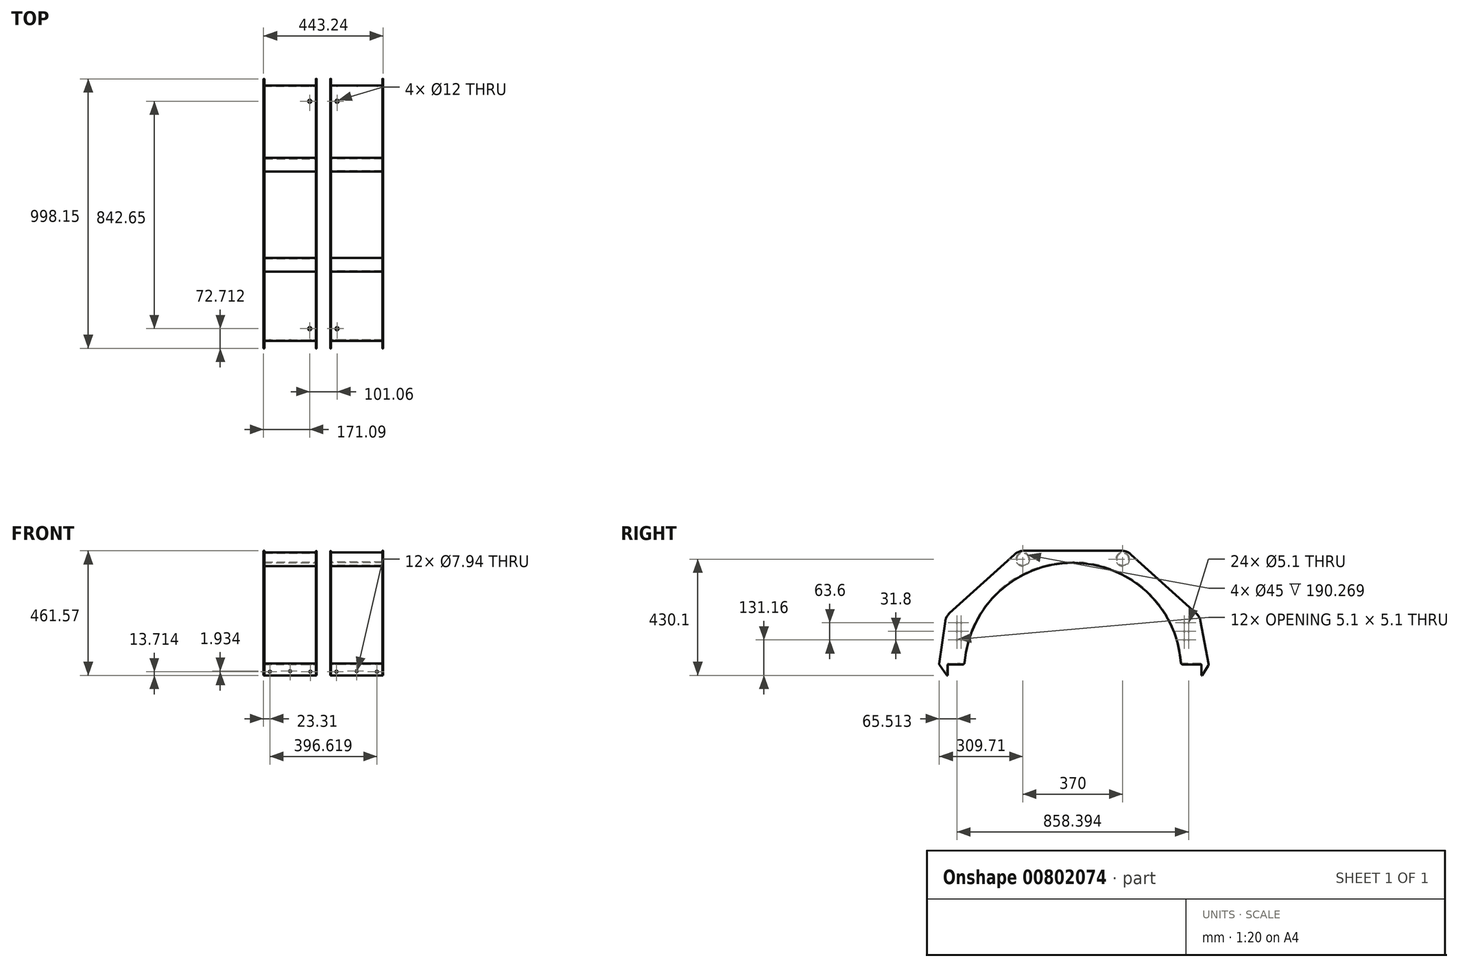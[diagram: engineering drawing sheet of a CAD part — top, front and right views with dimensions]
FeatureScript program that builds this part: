
annotation { "Feature Type Name" : "Feature", "Feature Type Description" : "" }
export const myFeature = defineFeature(function(context is Context, id is Id, definition is map)
    precondition{}
    {
        {
            var Q0;
            Q0=qCreatedBy(makeId("Right.planeOp"),FACE);
            var sketch = newSketch(context, id + "F0", { "sketchPlane" : qUnion([Q0])});
            skArc(sketch, "E0", {"start": v(-400.78, 31.26) * mm, "mid": v(0, 402) * mm, "end": v(400.78, 31.26) * mm});
            skLineSegment(sketch, "E1", {"start": v(-456.53, 215.37) * mm, "end": v(-216.59, 432.1) * mm});
            skLineSegment(sketch, "E2", {"start": v(457.5, 214.5) * mm, "end": v(216.59, 432.1) * mm});
            skLineSegment(sketch, "E3", {"start": v(183.07, 445) * mm, "end": v(-183.07, 445) * mm});
            skLineSegment(sketch, "E4", {"start": v(407.11, 25.4) * mm, "end": v(473.02, 25.4) * mm});
            skLineSegment(sketch, "E5", {"start": v(-460.32, 25.4) * mm, "end": v(-407.11, 25.4) * mm});
            skPoint(sketch, "E6.visualSharp", {"position": v(202.3, 445) * mm});
            skPoint(sketch, "E7.visualSharp", {"position": v(-401.2, 25.4) * mm});
            skArc(sketch, "E7.filletArc", {"start": v(-407.11, 25.4) * mm, "mid": v(-402.8, 27.09) * mm, "end": v(-400.78, 31.26) * mm});
            skPoint(sketch, "E8.visualSharp", {"position": v(401.2, 25.4) * mm});
            skArc(sketch, "E8.filletArc", {"start": v(400.78, 31.26) * mm, "mid": v(402.8, 27.09) * mm, "end": v(407.11, 25.4) * mm});
            skPoint(sketch, "E9.endSnap0", {"position": v(0, 402) * mm});
            skPoint(sketch, "E10", {"position": v(0, 445) * mm});
            skLineSegment(sketch, "E11", {"start": v(-472.53, 185.23) * mm, "end": v(-494.65, 27.9) * mm});
            skLineSegment(sketch, "E12", {"start": v(-493.54, 23.34) * mm, "end": v(-466.3, -15.1) * mm});
            skLineSegment(sketch, "E13", {"start": v(-463.5, -15.1) * mm, "end": v(-463.5, 22.22) * mm});
            skPoint(sketch, "E14.visualSharp", {"position": v(-470, 203.2) * mm});
            skArc(sketch, "E14.filletArc", {"start": v(-456.53, 215.37) * mm, "mid": v(-467.18, 201.7) * mm, "end": v(-472.53, 185.23) * mm});
            skPoint(sketch, "E15.visualSharp", {"position": v(-495, 25.4) * mm});
            skArc(sketch, "E15.filletArc", {"start": v(-494.65, 27.9) * mm, "mid": v(-494.53, 25.51) * mm, "end": v(-493.54, 23.34) * mm});
            skPoint(sketch, "E16.visualSharp", {"position": v(-463.5, 25.4) * mm});
            skArc(sketch, "E16.filletArc", {"start": v(-460.32, 25.4) * mm, "mid": v(-462.57, 24.47) * mm, "end": v(-463.5, 22.22) * mm});
            skLineSegment(sketch, "E17", {"start": v(476.2, 22.22) * mm, "end": v(476.2, -15.1) * mm});
            skPoint(sketch, "E18", {"position": v(505, 25.4) * mm});
            skLineSegment(sketch, "E19", {"start": v(479.37, -15.1) * mm, "end": v(502.46, 21.38) * mm});
            skLineSegment(sketch, "E20", {"start": v(503.33, 25.95) * mm, "end": v(473.12, 186.63) * mm});
            skPoint(sketch, "E21.visualSharp", {"position": v(470, 203.2) * mm});
            skArc(sketch, "E21.filletArc", {"start": v(473.12, 186.63) * mm, "mid": v(467.59, 201.85) * mm, "end": v(457.5, 214.5) * mm});
            skArc(sketch, "E22.filletArc", {"start": v(502.46, 21.38) * mm, "mid": v(503.33, 23.59) * mm, "end": v(503.33, 25.95) * mm});
            skLineSegment(sketch, "E23", {"start": v(476.2, -15.1) * mm, "end": v(479.37, -15.1) * mm});
            skLineSegment(sketch, "E24", {"start": v(-466.3, -15.1) * mm, "end": v(-463.5, -15.1) * mm});
            skPoint(sketch, "E25.visualSharp", {"position": v(476.2, 25.4) * mm});
            skArc(sketch, "E25.filletArc", {"start": v(476.2, 22.22) * mm, "mid": v(475.27, 24.47) * mm, "end": v(473.02, 25.4) * mm});
            skPoint(sketch, "E26", {"position": v(-429.2, 116.06) * mm});
            skPoint(sketch, "E27", {"position": v(-413.2, 116.06) * mm});
            skPoint(sketch, "E28", {"position": v(-413.2, 147.86) * mm});
            skPoint(sketch, "E29", {"position": v(-429.2, 147.86) * mm});
            skPoint(sketch, "E30", {"position": v(-429.2, 179.66) * mm});
            skPoint(sketch, "E31", {"position": v(-413.2, 179.66) * mm});
            skPoint(sketch, "E32", {"position": v(413.2, 179.66) * mm});
            skPoint(sketch, "E33", {"position": v(429.2, 179.66) * mm});
            skPoint(sketch, "E34", {"position": v(429.2, 147.86) * mm});
            skPoint(sketch, "E35", {"position": v(413.2, 147.86) * mm});
            skPoint(sketch, "E36", {"position": v(413.2, 116.06) * mm});
            skPoint(sketch, "E37", {"position": v(429.2, 116.06) * mm});
            skLineSegment(sketch, "E38.bottom", {"start": v(413.2, 179.66) * mm, "end": v(429.2, 179.66) * mm, "construction": true});
            skLineSegment(sketch, "E38.top", {"start": v(413.2, 116.06) * mm, "end": v(429.2, 116.06) * mm, "construction": true});
            skLineSegment(sketch, "E38.left", {"start": v(413.2, 179.66) * mm, "end": v(413.2, 116.06) * mm, "construction": true});
            skLineSegment(sketch, "E38.right", {"start": v(429.2, 179.66) * mm, "end": v(429.2, 116.06) * mm, "construction": true});
            skLineSegment(sketch, "E39", {"start": v(0, 0) * mm, "end": v(0, 524.96) * mm, "construction": true});
            skPoint(sketch, "E40.visualSharp", {"position": v(-202.31, 445) * mm});
            skArc(sketch, "E40.filletArc", {"start": v(-183.07, 445) * mm, "mid": v(-201.03, 441.66) * mm, "end": v(-216.59, 432.1) * mm});
            skPoint(sketch, "E41.newPointB", {"position": v(202.31, 445) * mm});
            skArc(sketch, "E41.filletArc", {"start": v(216.59, 432.1) * mm, "mid": v(201.03, 441.66) * mm, "end": v(183.07, 445) * mm});
            skSolve(sketch);
        }
        {
            var Q0;
            Q0 = qSketchRegion(id + "F0", true);
            extrude(context, id + "F1", {"entities" : qUnion([Q0]), "depth" : 3.17 * mm});
        }
        {
            var Q0;
            Q0=makeQuery(id+"F1.opExtrude","CAP_FACE",FACE,{"disambiguationData":[OSD([sQuery(id+"F0.wireOp",EDGE,"E0"),sQuery(id+"F0.wireOp",EDGE,"E9loCTzL-wOmK-y6Et-Pe2N-kgU0UY5jq1ZF"),sQuery(id+"F0.wireOp",EDGE,"E1"),sQuery(id+"F0.wireOp",EDGE,"s9JNnq10-T5jz-dtBx-Jel8-L66kQnyxZmdq"),sQuery(id+"F0.wireOp",EDGE,"E2"),sQuery(id+"F0.wireOp",EDGE,"E3"),sQuery(id+"F0.wireOp",EDGE,"E4"),sQuery(id+"F0.wireOp",EDGE,"E5"),sQuery(id+"F0.wireOp",EDGE,"86fa77fb-b35d-4607-8103-cc9440c46565.filletArc"),sQuery(id+"F0.wireOp",EDGE,"56854ff8-0e41-4e1b-8477-ec3efaea42f3.filletArc"),sQuery(id+"F0.wireOp",EDGE,"E6.filletArc"),sQuery(id+"F0.wireOp",EDGE,"a73865e9-f12d-4e8d-86f3-43cc75951e77.filletArc")])],"isStart":false});
            var sketch = newSketch(context, id + "F2", { "sketchPlane" : qUnion([Q0])});
            skArc(sketch, "E42", {"start": v(-400.78, 31.26) * mm, "mid": v(0, 402) * mm, "end": v(400.78, 31.26) * mm});
            skArc(sketch, "E43", {"start": v(-403.95, 31.5) * mm, "mid": v(0, 405.18) * mm, "end": v(403.95, 31.5) * mm});
            skLineSegment(sketch, "E44", {"start": v(-460.32, 28.57) * mm, "end": v(-407.11, 28.57) * mm});
            skLineSegment(sketch, "E45", {"start": v(-460.32, 25.4) * mm, "end": v(-407.11, 25.4) * mm});
            skArc(sketch, "E46.filletArc", {"start": v(-407.11, 25.4) * mm, "mid": v(-402.8, 27.09) * mm, "end": v(-400.78, 31.26) * mm});
            skArc(sketch, "E47.filletArc", {"start": v(-407.11, 28.57) * mm, "mid": v(-404.96, 29.42) * mm, "end": v(-403.95, 31.5) * mm});
            skLineSegment(sketch, "E48", {"start": v(473.02, 28.58) * mm, "end": v(407.11, 28.57) * mm});
            skLineSegment(sketch, "E49", {"start": v(473.02, 25.4) * mm, "end": v(407.11, 25.4) * mm});
            skArc(sketch, "E50.filletArc", {"start": v(400.78, 31.26) * mm, "mid": v(402.8, 27.09) * mm, "end": v(407.11, 25.4) * mm});
            skArc(sketch, "E51.filletArc", {"start": v(403.95, 31.5) * mm, "mid": v(404.96, 29.42) * mm, "end": v(407.11, 28.57) * mm});
            skLineSegment(sketch, "E52", {"start": v(-466.67, 22.22) * mm, "end": v(-466.67, -15.1) * mm});
            skLineSegment(sketch, "E53", {"start": v(-463.5, 22.22) * mm, "end": v(-463.5, -15.1) * mm});
            skLineSegment(sketch, "E54", {"start": v(-463.5, -15.1) * mm, "end": v(-466.67, -15.1) * mm});
            skPoint(sketch, "E55.visualSharp", {"position": v(-463.5, 25.4) * mm});
            skArc(sketch, "E55.filletArc", {"start": v(-460.32, 25.4) * mm, "mid": v(-462.57, 24.47) * mm, "end": v(-463.5, 22.22) * mm});
            skPoint(sketch, "E56.visualSharp", {"position": v(-466.67, 28.57) * mm});
            skArc(sketch, "E56.filletArc", {"start": v(-460.32, 28.57) * mm, "mid": v(-464.81, 26.72) * mm, "end": v(-466.67, 22.22) * mm});
            skLineSegment(sketch, "E57", {"start": v(476.2, 22.23) * mm, "end": v(476.2, -15.1) * mm});
            skLineSegment(sketch, "E58", {"start": v(476.2, -15.1) * mm, "end": v(479.37, -15.1) * mm});
            skLineSegment(sketch, "E59", {"start": v(479.37, -15.1) * mm, "end": v(479.37, 22.23) * mm});
            skPoint(sketch, "E60.visualSharp", {"position": v(476.2, 25.4) * mm});
            skArc(sketch, "E60.filletArc", {"start": v(476.2, 22.23) * mm, "mid": v(475.27, 24.47) * mm, "end": v(473.02, 25.4) * mm});
            skPoint(sketch, "E61.visualSharp", {"position": v(479.37, 28.58) * mm});
            skArc(sketch, "E61.filletArc", {"start": v(479.37, 22.23) * mm, "mid": v(477.51, 26.72) * mm, "end": v(473.02, 28.58) * mm});
            skSolve(sketch);
        }
        {
            var Q0;
            Q0 = qSketchRegion(id + "F2", true);
            extrude(context, id + "F3", {"entities" : qUnion([Q0]), "operationType" : NewBodyOperationType.ADD, "depth" : 190.27 * mm});
        }
        {
            var Q0;
            Q0=makeQuery(id+"F3.opExtrude","CAP_FACE",FACE,{"disambiguationData":[OSD([sQuery(id+"F2.wireOp",EDGE,"E42"),sQuery(id+"F2.wireOp",EDGE,"E43"),sQuery(id+"F2.wireOp",EDGE,"Qj5uD3Kj-Tnei-hYOQ-ZmSB-v0AgtbXvPEYO"),sQuery(id+"F2.wireOp",EDGE,"4pAmY6wd-Oeoi-wrFi-XpuQ-VInCCUa1Rv9z")])],"isStart":false});
            var sketch = newSketch(context, id + "F4", { "sketchPlane" : qUnion([Q0])});
            skArc(sketch, "E62", {"start": v(-400.78, 31.26) * mm, "mid": v(0, 402) * mm, "end": v(400.78, 31.26) * mm});
            skLineSegment(sketch, "E63", {"start": v(-456.31, 215.56) * mm, "end": v(-215.19, 433.37) * mm});
            skLineSegment(sketch, "E64", {"start": v(457.3, 214.68) * mm, "end": v(215.19, 433.37) * mm});
            skLineSegment(sketch, "E65", {"start": v(181.14, 446.47) * mm, "end": v(-181.14, 446.47) * mm});
            skPoint(sketch, "E66.visualSharp", {"position": v(-200.68, 446.47) * mm});
            skArc(sketch, "E66.filletArc", {"start": v(-181.14, 446.47) * mm, "mid": v(-199.38, 443.08) * mm, "end": v(-215.19, 433.37) * mm});
            skPoint(sketch, "E67.visualSharp", {"position": v(200.68, 446.47) * mm});
            skArc(sketch, "E67.filletArc", {"start": v(215.19, 433.37) * mm, "mid": v(199.38, 443.08) * mm, "end": v(181.14, 446.47) * mm});
            skPoint(sketch, "E68.visualSharp", {"position": v(398.78, 50.8) * mm});
            skLineSegment(sketch, "E69", {"start": v(0, 0) * mm, "end": v(0.42, 473.33) * mm, "construction": true});
            skPoint(sketch, "E69.endSnap0", {"position": v(0.42, 402) * mm});
            skLineSegment(sketch, "E70", {"start": v(-472.57, 184.94) * mm, "end": v(-494.65, 27.9) * mm});
            skArc(sketch, "E71.filletArc", {"start": v(-456.31, 215.56) * mm, "mid": v(-467.13, 201.68) * mm, "end": v(-472.57, 184.94) * mm});
            skLineSegment(sketch, "E72", {"start": v(473.17, 186.37) * mm, "end": v(503.33, 25.95) * mm});
            skArc(sketch, "E73.filletArc", {"start": v(473.17, 186.37) * mm, "mid": v(467.55, 201.83) * mm, "end": v(457.3, 214.68) * mm});
            skLineSegment(sketch, "E74", {"start": v(407.11, 25.4) * mm, "end": v(473.02, 25.4) * mm});
            skPoint(sketch, "E74.endSnap0", {"position": v(440.07, 25.4) * mm});
            skLineSegment(sketch, "E75", {"start": v(476.2, 22.22) * mm, "end": v(476.2, -15.1) * mm});
            skPoint(sketch, "E76.newPointA", {"position": v(481.52, 25.4) * mm});
            skArc(sketch, "E76.filletArc", {"start": v(476.2, 22.22) * mm, "mid": v(475.27, 24.47) * mm, "end": v(473.02, 25.4) * mm});
            skLineSegment(sketch, "E77", {"start": v(-407.11, 25.4) * mm, "end": v(-460.32, 25.4) * mm});
            skArc(sketch, "E78.filletArc", {"start": v(502.46, 21.38) * mm, "mid": v(503.33, 23.59) * mm, "end": v(503.33, 25.95) * mm});
            skLineSegment(sketch, "E79", {"start": v(-463.5, 22.22) * mm, "end": v(-463.5, -14.56) * mm});
            skLineSegment(sketch, "E80", {"start": v(-493.54, 23.34) * mm, "end": v(-466.67, -14.56) * mm});
            skPoint(sketch, "E81.newPointA", {"position": v(-497.1, 28.36) * mm});
            skPoint(sketch, "E81.newPointB", {"position": v(-494.58, 28.36) * mm});
            skArc(sketch, "E81.filletArc", {"start": v(-494.65, 27.9) * mm, "mid": v(-494.53, 25.51) * mm, "end": v(-493.54, 23.34) * mm});
            skArc(sketch, "E82.filletArc", {"start": v(-407.11, 25.4) * mm, "mid": v(-402.8, 27.09) * mm, "end": v(-400.78, 31.26) * mm});
            skArc(sketch, "E83.filletArc", {"start": v(400.78, 31.26) * mm, "mid": v(402.8, 27.09) * mm, "end": v(407.11, 25.4) * mm});
            skArc(sketch, "E84.filletArc", {"start": v(-460.32, 25.4) * mm, "mid": v(-462.57, 24.47) * mm, "end": v(-463.5, 22.22) * mm});
            skLineSegment(sketch, "E85", {"start": v(479.37, -15.1) * mm, "end": v(476.2, -15.1) * mm});
            skLineSegment(sketch, "E86.trimOffspring", {"start": v(479.37, -15.1) * mm, "end": v(502.46, 21.38) * mm});
            skLineSegment(sketch, "E87", {"start": v(-466.67, -14.56) * mm, "end": v(-463.5, -14.56) * mm});
            skSolve(sketch);
        }
        {
            var Q0;
            Q0 = qSketchRegion(id + "F4", true);
            extrude(context, id + "F5", {"entities" : qUnion([Q0]), "operationType" : NewBodyOperationType.ADD, "depth" : 3.17 * mm});
        }
        {
            var Q0;
            Q0=makeQuery(id+"F1.opExtrude","CAP_FACE",FACE,{"disambiguationData":[OSD([sQuery(id+"F0.wireOp",EDGE,"E0"),sQuery(id+"F0.wireOp",EDGE,"E9loCTzL-wOmK-y6Et-Pe2N-kgU0UY5jq1ZF"),sQuery(id+"F0.wireOp",EDGE,"E1"),sQuery(id+"F0.wireOp",EDGE,"s9JNnq10-T5jz-dtBx-Jel8-L66kQnyxZmdq"),sQuery(id+"F0.wireOp",EDGE,"E2"),sQuery(id+"F0.wireOp",EDGE,"E3"),sQuery(id+"F0.wireOp",EDGE,"E4"),sQuery(id+"F0.wireOp",EDGE,"E5"),sQuery(id+"F0.wireOp",EDGE,"86fa77fb-b35d-4607-8103-cc9440c46565.filletArc"),sQuery(id+"F0.wireOp",EDGE,"56854ff8-0e41-4e1b-8477-ec3efaea42f3.filletArc"),sQuery(id+"F0.wireOp",EDGE,"E6.filletArc"),sQuery(id+"F0.wireOp",EDGE,"a73865e9-f12d-4e8d-86f3-43cc75951e77.filletArc")])],"isStart":false});
            var sketch = newSketch(context, id + "F6", { "sketchPlane" : qUnion([Q0])});
            skCircle(sketch, "E88", {"center": v(185, 415) * mm, "radius": 25.4 * mm});
            skCircle(sketch, "E89", {"center": v(185, 415) * mm, "radius": 22.5 * mm});
            skCircle(sketch, "E90", {"center": v(-185, 415) * mm, "radius": 25.4 * mm});
            skCircle(sketch, "E91", {"center": v(-185, 415) * mm, "radius": 22.5 * mm});
            skSolve(sketch);
        }
        {
            var Q0;
            Q0 = qSketchRegion(id + "F6", true);
            extrude(context, id + "F7", {"entities" : qUnion([Q0]), "operationType" : NewBodyOperationType.ADD, "depth" : 190.27 * mm});
        }
        {
            var Q0;
            Q0=sQuery(id+"F0.wireOp",VERTEX,"E33");
            var Q1;
            Q1=sQuery(id+"F0.wireOp",VERTEX,"E32");
            var Q2;
            Q2=sQuery(id+"F0.wireOp",VERTEX,"E35");
            var Q3;
            Q3=sQuery(id+"F0.wireOp",VERTEX,"E34");
            var Q4;
            Q4=sQuery(id+"F0.wireOp",VERTEX,"E37");
            var Q5;
            Q5=sQuery(id+"F0.wireOp",VERTEX,"E36");
            var Q6;
            Q6=sQuery(id+"F0.wireOp",VERTEX,"E31");
            var Q7;
            Q7=sQuery(id+"F0.wireOp",VERTEX,"E30");
            var Q8;
            Q8=sQuery(id+"F0.wireOp",VERTEX,"E29");
            var Q9;
            Q9=sQuery(id+"F0.wireOp",VERTEX,"E28");
            var Q10;
            Q10=sQuery(id+"F0.wireOp",VERTEX,"E27");
            var Q11;
            Q11=sQuery(id+"F0.wireOp",VERTEX,"E26");
            var Q12;
            Q12=makeQuery(id+"F1.opExtrude","SWEPT_BODY",BODY,{"disambiguationData":[OSD([sQuery(id+"F0.wireOp",EDGE,"E0"),sQuery(id+"F0.wireOp",EDGE,"E1"),sQuery(id+"F0.wireOp",EDGE,"E2"),sQuery(id+"F0.wireOp",EDGE,"E3"),sQuery(id+"F0.wireOp",EDGE,"E4"),sQuery(id+"F0.wireOp",EDGE,"E5"),sQuery(id+"F0.wireOp",EDGE,"56854ff8-0e41-4e1b-8477-ec3efaea42f3.filletArc"),sQuery(id+"F0.wireOp",EDGE,"E6.filletArc"),sQuery(id+"F0.wireOp",EDGE,"E7.filletArc"),sQuery(id+"F0.wireOp",EDGE,"E8.filletArc"),sQuery(id+"F0.wireOp",EDGE,"E11"),sQuery(id+"F0.wireOp",EDGE,"E12"),sQuery(id+"F0.wireOp",EDGE,"E13"),sQuery(id+"F0.wireOp",EDGE,"E14.filletArc"),sQuery(id+"F0.wireOp",EDGE,"E15.filletArc"),sQuery(id+"F0.wireOp",EDGE,"E16.filletArc"),sQuery(id+"F0.wireOp",EDGE,"E17"),sQuery(id+"F0.wireOp",EDGE,"E19"),sQuery(id+"F0.wireOp",EDGE,"E20"),sQuery(id+"F0.wireOp",EDGE,"E21.filletArc"),sQuery(id+"F0.wireOp",EDGE,"E22.filletArc"),sQuery(id+"F0.wireOp",EDGE,"E23"),sQuery(id+"F0.wireOp",EDGE,"E24"),sQuery(id+"F0.wireOp",EDGE,"E25.filletArc")])]});
            hole(context, id + "F8", {"style" : HoleStyle.SIMPLE, "endStyle" : HoleEndStyle.BLIND, "oppositeDirection" : true, "holeDiameter" : 5.1 * mm, "holeDepth" : 17.75 * mm, "isTappedThrough" : true, "tappedDepth" : 10.25 * mm, "tapClearance" : 3, "startFromSketch" : true, "locations" : qUnion([Q0, Q1, Q2, Q3, Q4, Q5, Q6, Q7, Q8, Q9, Q10, Q11]), "scope" : qUnion([Q12])});
        }
        {
            var Q0;
            Q0=qCreatedBy(makeId("Right.planeOp"),FACE);
            cPlane(context, id + "F9", {"entities" : qUnion([Q0]), "cplaneType" : CPlaneType.OFFSET, "offset" : 25 * mm, "oppositeDirection" : true, "width" : 150 * mm, "height" : 150 * mm});
        }
        {
            var Q0;
            Q0=makeQuery(id+"F1.opExtrude","SWEPT_BODY",BODY,{"disambiguationData":[OSD([sQuery(id+"F0.wireOp",EDGE,"E0"),sQuery(id+"F0.wireOp",EDGE,"E1"),sQuery(id+"F0.wireOp",EDGE,"E2"),sQuery(id+"F0.wireOp",EDGE,"E3"),sQuery(id+"F0.wireOp",EDGE,"E4"),sQuery(id+"F0.wireOp",EDGE,"E5"),sQuery(id+"F0.wireOp",EDGE,"56854ff8-0e41-4e1b-8477-ec3efaea42f3.filletArc"),sQuery(id+"F0.wireOp",EDGE,"E6.filletArc"),sQuery(id+"F0.wireOp",EDGE,"E7.filletArc"),sQuery(id+"F0.wireOp",EDGE,"E8.filletArc"),sQuery(id+"F0.wireOp",EDGE,"E11"),sQuery(id+"F0.wireOp",EDGE,"E12"),sQuery(id+"F0.wireOp",EDGE,"E13"),sQuery(id+"F0.wireOp",EDGE,"E14.filletArc"),sQuery(id+"F0.wireOp",EDGE,"E15.filletArc"),sQuery(id+"F0.wireOp",EDGE,"E16.filletArc"),sQuery(id+"F0.wireOp",EDGE,"E17"),sQuery(id+"F0.wireOp",EDGE,"E19"),sQuery(id+"F0.wireOp",EDGE,"E20"),sQuery(id+"F0.wireOp",EDGE,"E21.filletArc"),sQuery(id+"F0.wireOp",EDGE,"E22.filletArc"),sQuery(id+"F0.wireOp",EDGE,"E23"),sQuery(id+"F0.wireOp",EDGE,"E24"),sQuery(id+"F0.wireOp",EDGE,"E25.filletArc")])]});
            var Q1;
            Q1=qCreatedBy(id+"F9.planeOp",FACE);
            mirror(context, id + "F10", {"entities" : qUnion([Q0]), "mirrorPlane" : qUnion([Q1])});
        }
        {
            var Q0;
            Q0=makeQuery(id+"F10.opPattern","COPY",BODY,{"derivedFrom":makeQuery(id+"F1.opExtrude","SWEPT_BODY",BODY,{"disambiguationData":[OSD([sQuery(id+"F0.wireOp",EDGE,"E0"),sQuery(id+"F0.wireOp",EDGE,"E1"),sQuery(id+"F0.wireOp",EDGE,"E2"),sQuery(id+"F0.wireOp",EDGE,"E3"),sQuery(id+"F0.wireOp",EDGE,"E4"),sQuery(id+"F0.wireOp",EDGE,"E5"),sQuery(id+"F0.wireOp",EDGE,"56854ff8-0e41-4e1b-8477-ec3efaea42f3.filletArc"),sQuery(id+"F0.wireOp",EDGE,"E6.filletArc"),sQuery(id+"F0.wireOp",EDGE,"E7.filletArc"),sQuery(id+"F0.wireOp",EDGE,"E8.filletArc"),sQuery(id+"F0.wireOp",EDGE,"E11"),sQuery(id+"F0.wireOp",EDGE,"E12"),sQuery(id+"F0.wireOp",EDGE,"E13"),sQuery(id+"F0.wireOp",EDGE,"E14.filletArc"),sQuery(id+"F0.wireOp",EDGE,"E15.filletArc"),sQuery(id+"F0.wireOp",EDGE,"E16.filletArc"),sQuery(id+"F0.wireOp",EDGE,"E17"),sQuery(id+"F0.wireOp",EDGE,"E19"),sQuery(id+"F0.wireOp",EDGE,"E20"),sQuery(id+"F0.wireOp",EDGE,"E21.filletArc"),sQuery(id+"F0.wireOp",EDGE,"E22.filletArc"),sQuery(id+"F0.wireOp",EDGE,"E23"),sQuery(id+"F0.wireOp",EDGE,"E24"),sQuery(id+"F0.wireOp",EDGE,"E25.filletArc")])]}),"instanceName":"1"});
            deleteBodies(context, id + "F11", {"entities" : qUnion([Q0])});
        }
        {
            var Q0;
            Q0=makeQuery(id+"F3.opExtrude","SWEPT_FACE",FACE,{"disambiguationData":[OSD([sQuery(id+"F2.wireOp",EDGE,"E52")])]});
            var sketch = newSketch(context, id + "F12", { "sketchPlane" : qUnion([Q0])});
            skLineSegment(sketch, "E92", {"start": v(-18.58, -1.39) * mm, "end": v(188.45, -1.39) * mm, "construction": true});
            skLineSegment(sketch, "E93", {"start": v(23.3, -19.94) * mm, "end": v(23.3, 12.68) * mm, "construction": true});
            skLineSegment(sketch, "E94", {"start": v(173.3, -20.85) * mm, "end": v(173.3, 12.98) * mm, "construction": true});
            skPoint(sketch, "E95", {"position": v(23.3, -1.39) * mm});
            skPoint(sketch, "E96", {"position": v(98.3, -1.39) * mm});
            skPoint(sketch, "E97", {"position": v(173.3, -1.39) * mm});
            skPoint(sketch, "E98", {"position": v(98.3, 0.55) * mm});
            skSolve(sketch);
        }
        {
            var Q0;
            Q0=sQuery(id+"F12.wireOp",VERTEX,"E95");
            var Q1;
            Q1=sQuery(id+"F12.wireOp",VERTEX,"E97");
            var Q2;
            Q2=sQuery(id+"F12.wireOp",VERTEX,"E98");
            var Q3;
            Q3=makeQuery(id+"F1.opExtrude","SWEPT_BODY",BODY,{"disambiguationData":[OSD([sQuery(id+"F0.wireOp",EDGE,"E0"),sQuery(id+"F0.wireOp",EDGE,"E1"),sQuery(id+"F0.wireOp",EDGE,"E2"),sQuery(id+"F0.wireOp",EDGE,"E3"),sQuery(id+"F0.wireOp",EDGE,"E4"),sQuery(id+"F0.wireOp",EDGE,"E5"),sQuery(id+"F0.wireOp",EDGE,"56854ff8-0e41-4e1b-8477-ec3efaea42f3.filletArc"),sQuery(id+"F0.wireOp",EDGE,"E6.filletArc"),sQuery(id+"F0.wireOp",EDGE,"E7.filletArc"),sQuery(id+"F0.wireOp",EDGE,"E8.filletArc"),sQuery(id+"F0.wireOp",EDGE,"E11"),sQuery(id+"F0.wireOp",EDGE,"E12"),sQuery(id+"F0.wireOp",EDGE,"E13"),sQuery(id+"F0.wireOp",EDGE,"E14.filletArc"),sQuery(id+"F0.wireOp",EDGE,"E15.filletArc"),sQuery(id+"F0.wireOp",EDGE,"E16.filletArc"),sQuery(id+"F0.wireOp",EDGE,"E17"),sQuery(id+"F0.wireOp",EDGE,"E19"),sQuery(id+"F0.wireOp",EDGE,"E20"),sQuery(id+"F0.wireOp",EDGE,"E21.filletArc"),sQuery(id+"F0.wireOp",EDGE,"E22.filletArc"),sQuery(id+"F0.wireOp",EDGE,"E23"),sQuery(id+"F0.wireOp",EDGE,"E24"),sQuery(id+"F0.wireOp",EDGE,"E25.filletArc")])]});
            hole(context, id + "F13", {"style" : HoleStyle.SIMPLE, "endStyle" : HoleEndStyle.THROUGH, "holeDiameter" : 7.94 * mm, "isTappedThrough" : true, "tappedDepth" : 10.25 * mm, "tapClearance" : 3, "startFromSketch" : true, "locations" : qUnion([Q0, Q1, Q2]), "scope" : qUnion([Q3]), "majorDiameter" : 5 * mm});
        }
        {
            var Q0;
            Q0=makeQuery(id+"F1.opExtrude","SWEPT_BODY",BODY,{"disambiguationData":[OSD([sQuery(id+"F0.wireOp",EDGE,"E0"),sQuery(id+"F0.wireOp",EDGE,"E1"),sQuery(id+"F0.wireOp",EDGE,"E2"),sQuery(id+"F0.wireOp",EDGE,"E3"),sQuery(id+"F0.wireOp",EDGE,"E4"),sQuery(id+"F0.wireOp",EDGE,"E5"),sQuery(id+"F0.wireOp",EDGE,"56854ff8-0e41-4e1b-8477-ec3efaea42f3.filletArc"),sQuery(id+"F0.wireOp",EDGE,"E6.filletArc"),sQuery(id+"F0.wireOp",EDGE,"E7.filletArc"),sQuery(id+"F0.wireOp",EDGE,"E8.filletArc"),sQuery(id+"F0.wireOp",EDGE,"E11"),sQuery(id+"F0.wireOp",EDGE,"E12"),sQuery(id+"F0.wireOp",EDGE,"E13"),sQuery(id+"F0.wireOp",EDGE,"E14.filletArc"),sQuery(id+"F0.wireOp",EDGE,"E15.filletArc"),sQuery(id+"F0.wireOp",EDGE,"E16.filletArc"),sQuery(id+"F0.wireOp",EDGE,"E17"),sQuery(id+"F0.wireOp",EDGE,"E19"),sQuery(id+"F0.wireOp",EDGE,"E20"),sQuery(id+"F0.wireOp",EDGE,"E21.filletArc"),sQuery(id+"F0.wireOp",EDGE,"E22.filletArc"),sQuery(id+"F0.wireOp",EDGE,"E23"),sQuery(id+"F0.wireOp",EDGE,"E24"),sQuery(id+"F0.wireOp",EDGE,"E25.filletArc")])]});
            var Q1;
            Q1=qCreatedBy(id+"F9.planeOp",FACE);
            mirror(context, id + "F14", {"entities" : qUnion([Q0]), "mirrorPlane" : qUnion([Q1])});
        }
        {
            var Q0;
            Q0=makeQuery(id+"F3.opExtrude","SWEPT_FACE",FACE,{"disambiguationData":[OSD([sQuery(id+"F2.wireOp",EDGE,"E44")])]});
            var sketch = newSketch(context, id + "F15", { "sketchPlane" : qUnion([Q0])});
            skCircle(sketch, "E99", {"center": v(25.53, -422) * mm, "radius": 6 * mm});
            skSolve(sketch);
        }
        {
            var Q0;
            Q0 = qSketchRegion(id + "F15", true);
            extrude(context, id + "F16", {"entities" : qUnion([Q0]), "operationType" : NewBodyOperationType.REMOVE, "oppositeDirection" : true, "depth" : 25 * mm});
        }
        {
            var Q0;
            Q0=makeQuery(id+"F3.opExtrude","SWEPT_FACE",FACE,{"disambiguationData":[OSD([sQuery(id+"F2.wireOp",EDGE,"E48")])]});
            var sketch = newSketch(context, id + "F17", { "sketchPlane" : qUnion([Q0])});
            skCircle(sketch, "E100", {"center": v(25.53, 420.65) * mm, "radius": 6 * mm});
            skSolve(sketch);
        }
        {
            var Q0;
            Q0 = qSketchRegion(id + "F17", true);
            extrude(context, id + "F18", {"entities" : qUnion([Q0]), "operationType" : NewBodyOperationType.REMOVE, "oppositeDirection" : true, "depth" : 25 * mm});
        }
        {
            var Q0;
            Q0=makeQuery(id+"F14.opPattern","COPY",BODY,{"derivedFrom":makeQuery(id+"F1.opExtrude","SWEPT_BODY",BODY,{"disambiguationData":[OSD([sQuery(id+"F0.wireOp",EDGE,"E0"),sQuery(id+"F0.wireOp",EDGE,"E1"),sQuery(id+"F0.wireOp",EDGE,"E2"),sQuery(id+"F0.wireOp",EDGE,"E3"),sQuery(id+"F0.wireOp",EDGE,"E4"),sQuery(id+"F0.wireOp",EDGE,"E5"),sQuery(id+"F0.wireOp",EDGE,"56854ff8-0e41-4e1b-8477-ec3efaea42f3.filletArc"),sQuery(id+"F0.wireOp",EDGE,"E6.filletArc"),sQuery(id+"F0.wireOp",EDGE,"E7.filletArc"),sQuery(id+"F0.wireOp",EDGE,"E8.filletArc"),sQuery(id+"F0.wireOp",EDGE,"E11"),sQuery(id+"F0.wireOp",EDGE,"E12"),sQuery(id+"F0.wireOp",EDGE,"E13"),sQuery(id+"F0.wireOp",EDGE,"E14.filletArc"),sQuery(id+"F0.wireOp",EDGE,"E15.filletArc"),sQuery(id+"F0.wireOp",EDGE,"E16.filletArc"),sQuery(id+"F0.wireOp",EDGE,"E17"),sQuery(id+"F0.wireOp",EDGE,"E19"),sQuery(id+"F0.wireOp",EDGE,"E20"),sQuery(id+"F0.wireOp",EDGE,"E21.filletArc"),sQuery(id+"F0.wireOp",EDGE,"E22.filletArc"),sQuery(id+"F0.wireOp",EDGE,"E23"),sQuery(id+"F0.wireOp",EDGE,"E24"),sQuery(id+"F0.wireOp",EDGE,"E25.filletArc")])]}),"instanceName":"1"});
            deleteBodies(context, id + "F19", {"entities" : qUnion([Q0])});
        }
        {
            var Q0;
            Q0=makeQuery(id+"F1.opExtrude","SWEPT_BODY",BODY,{"disambiguationData":[OSD([sQuery(id+"F0.wireOp",EDGE,"E0"),sQuery(id+"F0.wireOp",EDGE,"E1"),sQuery(id+"F0.wireOp",EDGE,"E2"),sQuery(id+"F0.wireOp",EDGE,"E3"),sQuery(id+"F0.wireOp",EDGE,"E4"),sQuery(id+"F0.wireOp",EDGE,"E5"),sQuery(id+"F0.wireOp",EDGE,"56854ff8-0e41-4e1b-8477-ec3efaea42f3.filletArc"),sQuery(id+"F0.wireOp",EDGE,"E6.filletArc"),sQuery(id+"F0.wireOp",EDGE,"E7.filletArc"),sQuery(id+"F0.wireOp",EDGE,"E8.filletArc"),sQuery(id+"F0.wireOp",EDGE,"E11"),sQuery(id+"F0.wireOp",EDGE,"E12"),sQuery(id+"F0.wireOp",EDGE,"E13"),sQuery(id+"F0.wireOp",EDGE,"E14.filletArc"),sQuery(id+"F0.wireOp",EDGE,"E15.filletArc"),sQuery(id+"F0.wireOp",EDGE,"E16.filletArc"),sQuery(id+"F0.wireOp",EDGE,"E17"),sQuery(id+"F0.wireOp",EDGE,"E19"),sQuery(id+"F0.wireOp",EDGE,"E20"),sQuery(id+"F0.wireOp",EDGE,"E21.filletArc"),sQuery(id+"F0.wireOp",EDGE,"E22.filletArc"),sQuery(id+"F0.wireOp",EDGE,"E23"),sQuery(id+"F0.wireOp",EDGE,"E24"),sQuery(id+"F0.wireOp",EDGE,"E25.filletArc")])]});
            var Q1;
            Q1=qCreatedBy(id+"F9.planeOp",FACE);
            mirror(context, id + "F20", {"entities" : qUnion([Q0]), "mirrorPlane" : qUnion([Q1])});
        }
    });
